# Revit family: Festpunkt Typ FGL
name_source: partatom
category: HLS-Bauteile
revit_build: Autodesk Revit 2017 (Build: 20190507_1515(x64)
units: mm (PartAtom-declared; Revit-internal decimal feet)

## family parameters
Arbeitsebenenbasiert = Ja
Beim Laden mit Abzugskörper schneiden = Nein
Bemaßung runder Anschluss = Durchmesser verwenden
Gemeinsam genutzt = Ja
Immer vertikal = Nein
Raumberechnungspunkt = Nein
Teiletyp = Normal

## types (1)
- Festpunkt Typ FGL
    Anschluss = 1/2''
    Anschlusstyp = Muffe
    Anzahl Anschlüsse = 2
    Artikelnummer = 0770335
    Breite Platte = 80 mm  [stored 0.262467 ft]
    EAN = 4250928417534
    Fabrikat = MEFA
    Firma = MEFA Befestigungs- und Montagesysteme GmbH
    Gewicht = 0.53 kg
    Gewicht pro Bauteil = 0.53 kg
    Kurztext1 = Klemmfestpunkt FGL
    Kurztext2 = 2 x Muffe 1/2'' 1,4 kN
    Lochabstand = 56 mm
    Lochdurchmesser = 13 mm
    Länge Platte = 125 mm  [stored 0.410105 ft]
    Mengeneinheit = St
    Schalldämmeinlage = ohne Dämmung
    Stärke Platte = 6 mm  [stored 0.019685 ft]
    Vorgabe-Ansicht = 1219 mm
    max. Rohraußendurchmesser = 46 mm  [stored 0.150919 ft]
    max. Temperaturbeständigkeit = 100 °C
    min. Rohraußendurchmesser = 20 mm  [stored 0.0656168 ft]
    vpe = 1 St

note: [stored X ft] marks values corroborated as IEEE doubles in the binary element streams (Revit-internal decimal feet)

## geometry (parser evidence)
native form markers: Sweep x3
no freeform markers — native parametric forms only
